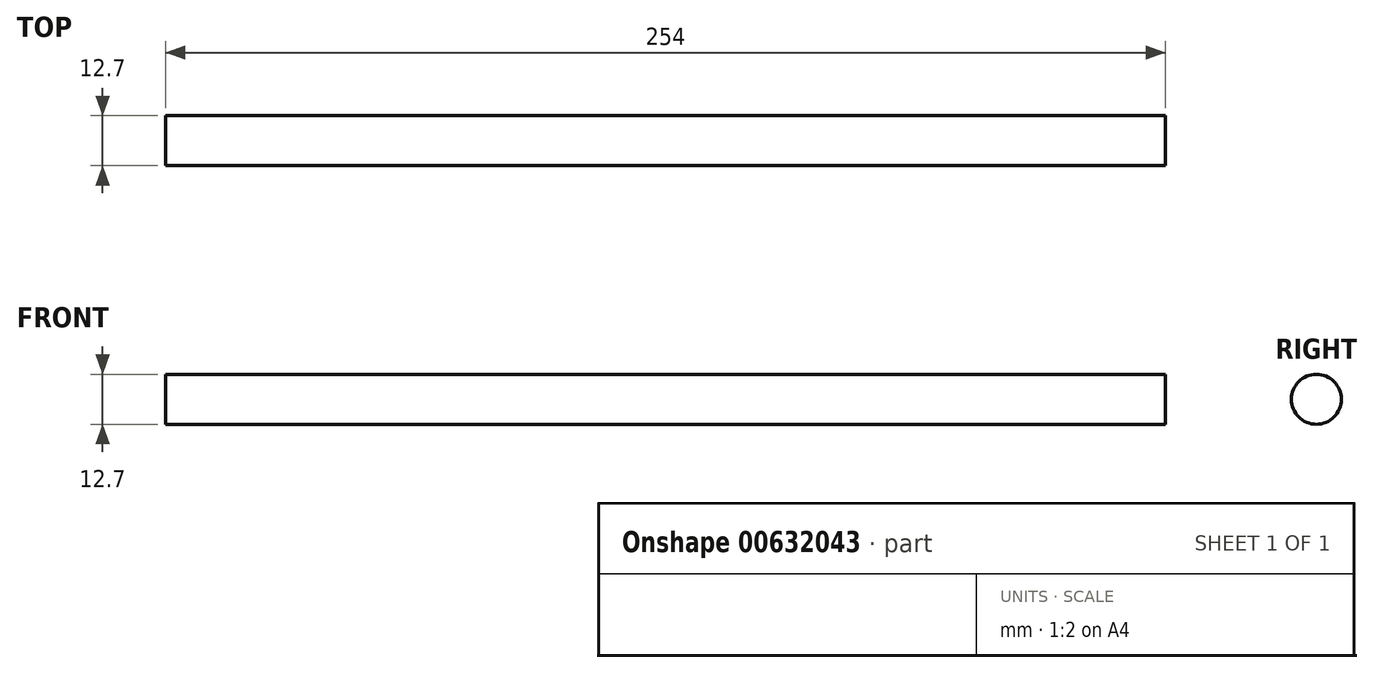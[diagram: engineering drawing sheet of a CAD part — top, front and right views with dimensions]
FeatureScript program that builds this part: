
annotation { "Feature Type Name" : "Feature", "Feature Type Description" : "" }
export const myFeature = defineFeature(function(context is Context, id is Id, definition is map)
    precondition{}
    {
        {
            var Q0;
            Q0=qCreatedBy(makeId("Right.planeOp"),FACE);
            var sketch = newSketch(context, id + "F0", { "sketchPlane" : qUnion([Q0])});
            skCircle(sketch, "E0", {"center": v(0, 0) * mm, "radius": 6.35 * mm});
            skSolve(sketch);
        }
        {
            var Q0;
            Q0 = qSketchRegion(id + "F0", true);
            extrude(context, id + "F1", {"entities" : qUnion([Q0]), "depth" : 254 * mm, "offsetDistance" : 25.4 * mm});
        }
    });
